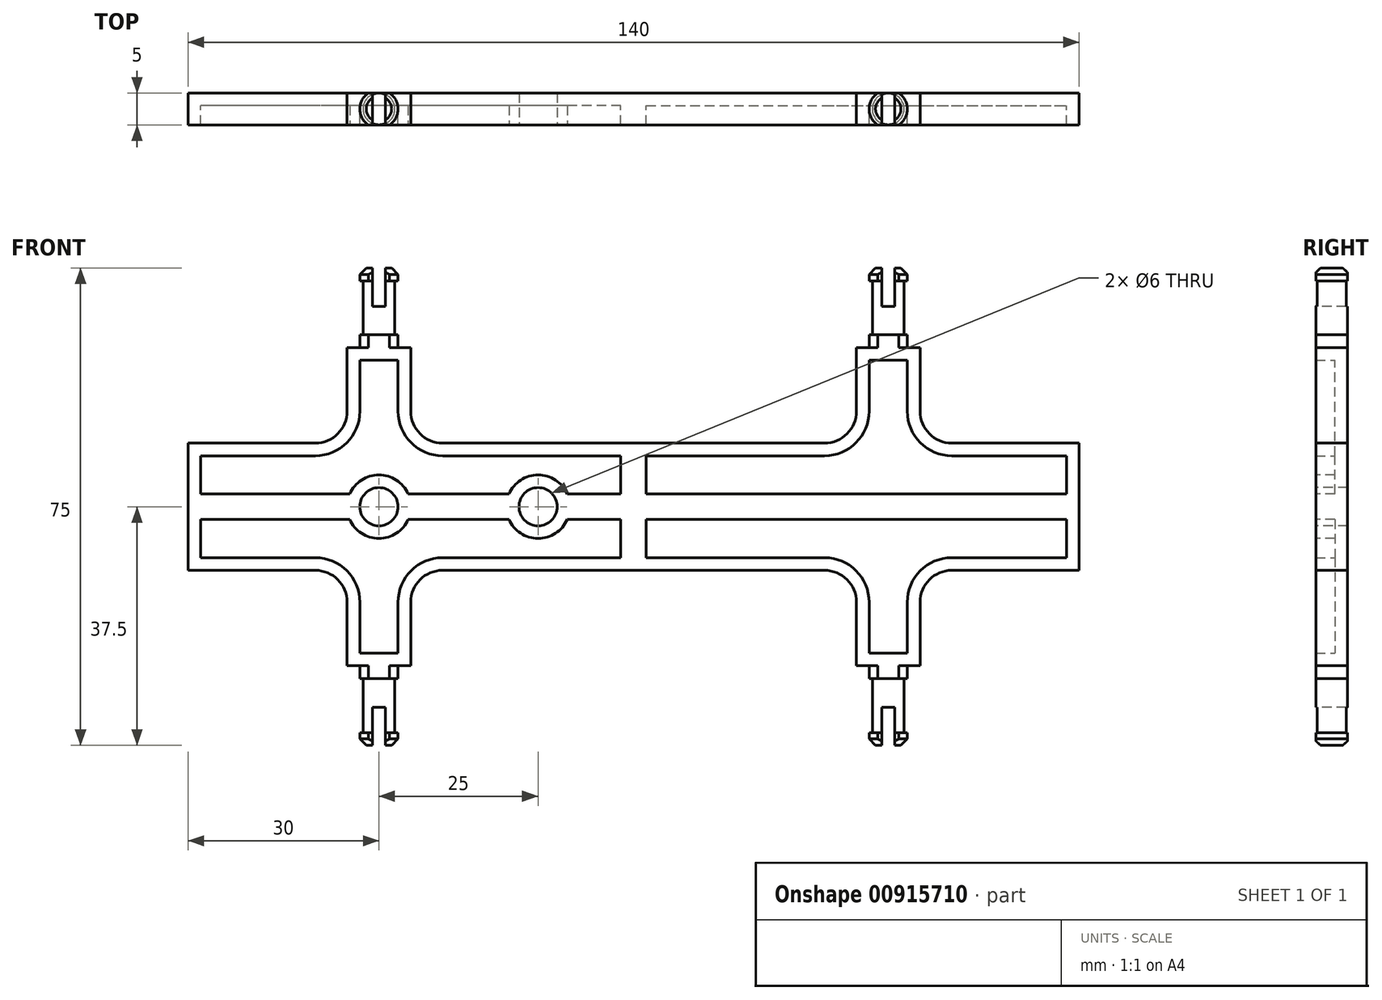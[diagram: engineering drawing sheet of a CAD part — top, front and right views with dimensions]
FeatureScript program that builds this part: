
annotation { "Feature Type Name" : "Feature", "Feature Type Description" : "" }
export const myFeature = defineFeature(function(context is Context, id is Id, definition is map)
    precondition{}
    {
        {
            var Q0;
            Q0=qCreatedBy(makeId("Front.planeOp"),FACE);
            var sketch = newSketch(context, id + "F0", { "sketchPlane" : qUnion([Q0])});
            skLineSegment(sketch, "E0.bottom", {"start": v(0, 0) * mm, "end": v(70, 0) * mm});
            skLineSegment(sketch, "E0.top", {"start": v(0, 10) * mm, "end": v(30, 10) * mm});
            skLineSegment(sketch, "E0.left", {"start": v(0, 0) * mm, "end": v(0, 10) * mm});
            skLineSegment(sketch, "E0.right", {"start": v(70, 0) * mm, "end": v(70, 10) * mm});
            skLineSegment(sketch, "E1.top", {"start": v(35, 25) * mm, "end": v(45, 25) * mm});
            skLineSegment(sketch, "E1.left", {"start": v(35, 15) * mm, "end": v(35, 25) * mm});
            skLineSegment(sketch, "E1.right", {"start": v(45, 15) * mm, "end": v(45, 25) * mm});
            skLineSegment(sketch, "E2.trimOffspring", {"start": v(50, 10) * mm, "end": v(70, 10) * mm});
            skPoint(sketch, "E3.visualSharp", {"position": v(35, 10) * mm});
            skArc(sketch, "E3.filletArc", {"start": v(30, 10) * mm, "mid": v(33.54, 11.46) * mm, "end": v(35, 15) * mm});
            skPoint(sketch, "E4.visualSharp", {"position": v(45, 10) * mm});
            skArc(sketch, "E4.filletArc", {"start": v(45, 15) * mm, "mid": v(46.46, 11.46) * mm, "end": v(50, 10) * mm});
            skSolve(sketch);
        }
        {
            var Q0;
            Q0 = qSketchRegion(id + "F0", true);
            extrude(context, id + "F1", {"entities" : qUnion([Q0]), "endBound" : BoundingType.SYMMETRIC, "depth" : 5 * mm, "offsetDistance" : 25 * mm});
        }
        {
            var Q0;
            Q0=makeQuery(id+"F1.opExtrude","CAP_FACE",FACE,{"disambiguationData":[OSD([sQuery(id+"F0.wireOp",EDGE,"E0.bottom"),sQuery(id+"F0.wireOp",EDGE,"E0.top"),sQuery(id+"F0.wireOp",EDGE,"E0.left"),sQuery(id+"F0.wireOp",EDGE,"E0.right"),sQuery(id+"F0.wireOp",EDGE,"E1.top"),sQuery(id+"F0.wireOp",EDGE,"E1.left"),sQuery(id+"F0.wireOp",EDGE,"E1.right"),sQuery(id+"F0.wireOp",EDGE,"E2.trimOffspring"),sQuery(id+"F0.wireOp",EDGE,"E3.filletArc"),sQuery(id+"F0.wireOp",EDGE,"E4.filletArc")])],"isStart":false});
            shell(context, id + "F2", {"entities" : qUnion([Q0]), "thickness" : 2 * mm});
        }
        {
            var Q0;
            Q0=qCreatedBy(makeId("Front.planeOp"),FACE);
            var sketch = newSketch(context, id + "F3", { "sketchPlane" : qUnion([Q0])});
            skLineSegment(sketch, "E5", {"start": v(40, 25) * mm, "end": v(40, 37.5) * mm});
            skLineSegment(sketch, "E6", {"start": v(40, 37.5) * mm, "end": v(37, 37.5) * mm});
            skLineSegment(sketch, "E7", {"start": v(37, 37.5) * mm, "end": v(37, 35.5) * mm});
            skLineSegment(sketch, "E8", {"start": v(37, 35.5) * mm, "end": v(37.5, 35.5) * mm});
            skLineSegment(sketch, "E9", {"start": v(37.5, 35.5) * mm, "end": v(37.5, 27) * mm});
            skLineSegment(sketch, "E10", {"start": v(37.5, 27) * mm, "end": v(37, 27) * mm});
            skLineSegment(sketch, "E11", {"start": v(37, 27) * mm, "end": v(37, 25) * mm});
            skLineSegment(sketch, "E12", {"start": v(37, 25) * mm, "end": v(40, 25) * mm});
            skSolve(sketch);
        }
        {
            var Q0;
            Q0 = qSketchRegion(id + "F3", true);
            var Q1;
            Q1=sQuery(id+"F3.wireOp",EDGE,"E5");
            revolve(context, id + "F4", {"operationType" : NewBodyOperationType.ADD, "surfaceOperationType" : NewSurfaceOperationType.NEW, "entities" : qUnion([Q0]), "axis" : qUnion([Q1]), "revolveType" : RevolveType.FULL});
        }
        {
            var Q0;
            Q0=makeQuery(id+"F4.opRevolve","SWEPT_EDGE",EDGE,{"disambiguationData":[OSD([sQuery(id+"F3.wireOp",EDGE,"E6"),sQuery(id+"F3.wireOp",EDGE,"E7")])]});
            chamfer(context, id + "F5", {"entities" : qUnion([Q0]), "width" : 1 * mm, "tangentPropagation" : true});
        }
        {
            var Q0;
            Q0=makeQuery(id+"F4.opRevolve","SWEPT_FACE",FACE,{"disambiguationData":[OSD([sQuery(id+"F3.wireOp",EDGE,"E6")])]});
            var sketch = newSketch(context, id + "F6", { "sketchPlane" : qUnion([Q0])});
            skLineSegment(sketch, "E13.bottom", {"start": v(-1.45, 2.5) * mm, "end": v(71.88, 2.5) * mm});
            skLineSegment(sketch, "E13.top", {"start": v(-1.45, -2.5) * mm, "end": v(71.88, -2.5) * mm});
            skLineSegment(sketch, "E13.left", {"start": v(-1.45, 2.5) * mm, "end": v(-1.45, -2.5) * mm});
            skLineSegment(sketch, "E13.right", {"start": v(71.88, 2.5) * mm, "end": v(71.88, -2.5) * mm});
            skSolve(sketch);
        }
        {
            var Q0;
            Q0 = qSketchRegion(id + "F6", true);
            extrude(context, id + "F7", {"entities" : qUnion([Q0]), "operationType" : NewBodyOperationType.INTERSECT, "endBound" : BoundingType.THROUGH_ALL, "oppositeDirection" : true, "depth" : 25 * mm, "offsetDistance" : 25 * mm});
        }
        {
            var Q0;
            Q0=makeQuery(id+"F4.opRevolve","SWEPT_FACE",FACE,{"disambiguationData":[OSD([sQuery(id+"F3.wireOp",EDGE,"E6")])]});
            var sketch = newSketch(context, id + "F8", { "sketchPlane" : qUnion([Q0])});
            skLineSegment(sketch, "E14.bottom", {"start": v(39, 2.85) * mm, "end": v(41, 2.85) * mm});
            skLineSegment(sketch, "E14.top", {"start": v(39, -3.9) * mm, "end": v(41, -3.9) * mm});
            skLineSegment(sketch, "E14.left", {"start": v(39, 2.85) * mm, "end": v(39, -3.9) * mm});
            skLineSegment(sketch, "E14.right", {"start": v(41, 2.85) * mm, "end": v(41, -3.9) * mm});
            skSolve(sketch);
        }
        {
            var Q0;
            Q0 = qSketchRegion(id + "F8", true);
            extrude(context, id + "F9", {"entities" : qUnion([Q0]), "operationType" : NewBodyOperationType.REMOVE, "oppositeDirection" : true, "depth" : 6 * mm, "offsetDistance" : 25 * mm});
        }
        {
            var Q0;
            Q0=makeQuery(id+"F1.opExtrude","SWEPT_BODY",BODY,{"disambiguationData":[OSD([sQuery(id+"F0.wireOp",EDGE,"E0.bottom"),sQuery(id+"F0.wireOp",EDGE,"E0.top"),sQuery(id+"F0.wireOp",EDGE,"E0.left"),sQuery(id+"F0.wireOp",EDGE,"E0.right"),sQuery(id+"F0.wireOp",EDGE,"E1.top"),sQuery(id+"F0.wireOp",EDGE,"E1.left"),sQuery(id+"F0.wireOp",EDGE,"E1.right"),sQuery(id+"F0.wireOp",EDGE,"E2.trimOffspring"),sQuery(id+"F0.wireOp",EDGE,"E3.filletArc"),sQuery(id+"F0.wireOp",EDGE,"E4.filletArc")])]});
            var Q1;
            Q1=qCreatedBy(makeId("Top.planeOp"),FACE);
            mirror(context, id + "F10", {"operationType" : NewBodyOperationType.ADD, "entities" : qUnion([Q0]), "mirrorPlane" : qUnion([Q1])});
        }
        {
            var Q0;
            Q0=makeQuery(id+"F1.opExtrude","SWEPT_BODY",BODY,{"disambiguationData":[OSD([sQuery(id+"F0.wireOp",EDGE,"E0.bottom"),sQuery(id+"F0.wireOp",EDGE,"E0.top"),sQuery(id+"F0.wireOp",EDGE,"E0.left"),sQuery(id+"F0.wireOp",EDGE,"E0.right"),sQuery(id+"F0.wireOp",EDGE,"E1.top"),sQuery(id+"F0.wireOp",EDGE,"E1.left"),sQuery(id+"F0.wireOp",EDGE,"E1.right"),sQuery(id+"F0.wireOp",EDGE,"E2.trimOffspring"),sQuery(id+"F0.wireOp",EDGE,"E3.filletArc"),sQuery(id+"F0.wireOp",EDGE,"E4.filletArc")])]});
            var Q1;
            Q1=qCreatedBy(makeId("Right.planeOp"),FACE);
            mirror(context, id + "F11", {"operationType" : NewBodyOperationType.ADD, "entities" : qUnion([Q0]), "mirrorPlane" : qUnion([Q1])});
        }
        {
            var Q0;
            {var subQ0=makeQuery(id+"F7.boolean.opBoolean","MERGE",FACE,{"derivedFrom":[makeQuery(id+"F1.opExtrude","CAP_FACE",FACE,{"disambiguationData":[OSD([sQuery(id+"F0.wireOp",EDGE,"E0.bottom"),sQuery(id+"F0.wireOp",EDGE,"E0.top"),sQuery(id+"F0.wireOp",EDGE,"E0.left"),sQuery(id+"F0.wireOp",EDGE,"E0.right"),sQuery(id+"F0.wireOp",EDGE,"E1.top"),sQuery(id+"F0.wireOp",EDGE,"E1.left"),sQuery(id+"F0.wireOp",EDGE,"E1.right"),sQuery(id+"F0.wireOp",EDGE,"E2.trimOffspring"),sQuery(id+"F0.wireOp",EDGE,"E3.filletArc"),sQuery(id+"F0.wireOp",EDGE,"E4.filletArc")])],"isStart":false})],"fromTools":[makeQuery(id+"F7.boolean.toolComplement.opBoolean","COPY",FACE,{"derivedFrom":makeQuery(id+"F7.opExtrude","SWEPT_FACE",FACE,{"disambiguationData":[OSD([sQuery(id+"F6.wireOp",EDGE,"E13.top")])]})})]});var subQ1=makeQuery(id+"F10.boolean.opBoolean","MERGE",FACE,{"derivedFrom":[subQ0,makeQuery(id+"F10.opPattern","COPY",FACE,{"derivedFrom":subQ0,"instanceName":"1"})]});Q0=makeQuery(id+"F11.boolean.opBoolean","MERGE",FACE,{"derivedFrom":[subQ1,makeQuery(id+"F11.opPattern","COPY",FACE,{"derivedFrom":subQ1,"instanceName":"1"})]});}
            var sketch = newSketch(context, id + "F12", { "sketchPlane" : qUnion([Q0])});
            skCircle(sketch, "E15", {"center": v(-40, 0) * mm, "radius": 5 * mm});
            skCircle(sketch, "E16", {"center": v(-15, 0) * mm, "radius": 5 * mm});
            skSolve(sketch);
        }
        {
            var Q0;
            Q0 = qSketchRegion(id + "F12", true);
            extrude(context, id + "F13", {"entities" : qUnion([Q0]), "operationType" : NewBodyOperationType.ADD, "endBound" : BoundingType.UP_TO_NEXT, "oppositeDirection" : true, "depth" : 4 * mm, "offsetDistance" : 25 * mm});
        }
        {
            var Q0;
            {var subQ0=makeQuery(id+"F7.boolean.opBoolean","MERGE",FACE,{"derivedFrom":[makeQuery(id+"F1.opExtrude","CAP_FACE",FACE,{"disambiguationData":[OSD([sQuery(id+"F0.wireOp",EDGE,"E0.bottom"),sQuery(id+"F0.wireOp",EDGE,"E0.top"),sQuery(id+"F0.wireOp",EDGE,"E0.left"),sQuery(id+"F0.wireOp",EDGE,"E0.right"),sQuery(id+"F0.wireOp",EDGE,"E1.top"),sQuery(id+"F0.wireOp",EDGE,"E1.left"),sQuery(id+"F0.wireOp",EDGE,"E1.right"),sQuery(id+"F0.wireOp",EDGE,"E2.trimOffspring"),sQuery(id+"F0.wireOp",EDGE,"E3.filletArc"),sQuery(id+"F0.wireOp",EDGE,"E4.filletArc")])],"isStart":false})],"fromTools":[makeQuery(id+"F7.boolean.toolComplement.opBoolean","COPY",FACE,{"derivedFrom":makeQuery(id+"F7.opExtrude","SWEPT_FACE",FACE,{"disambiguationData":[OSD([sQuery(id+"F6.wireOp",EDGE,"E13.top")])]})})]});var subQ1=makeQuery(id+"F10.boolean.opBoolean","MERGE",FACE,{"derivedFrom":[subQ0,makeQuery(id+"F10.opPattern","COPY",FACE,{"derivedFrom":subQ0,"instanceName":"1"})]});Q0=makeQuery(id+"F13.boolean.opBoolean","MERGE",FACE,{"derivedFrom":[makeQuery(id+"F11.boolean.opBoolean","MERGE",FACE,{"derivedFrom":[subQ1,makeQuery(id+"F11.opPattern","COPY",FACE,{"derivedFrom":subQ1,"instanceName":"1"})]}),makeQuery(id+"F13.opExtrude","CAP_FACE",FACE,{"disambiguationData":[OSD([sQuery(id+"F12.wireOp",EDGE,"E15")])],"isStart":true}),makeQuery(id+"F13.opExtrude","CAP_FACE",FACE,{"disambiguationData":[OSD([sQuery(id+"F12.wireOp",EDGE,"E16")])],"isStart":true})]});}
            var sketch = newSketch(context, id + "F14", { "sketchPlane" : qUnion([Q0])});
            skPoint(sketch, "E17", {"position": v(-40, 0) * mm});
            skPoint(sketch, "E18", {"position": v(-15, 0) * mm});
            skSolve(sketch);
        }
        {
            var Q0;
            Q0=sQuery(id+"F14.wireOp",VERTEX,"E17");
            var Q1;
            Q1=sQuery(id+"F14.wireOp",VERTEX,"E18");
            var Q2;
            Q2=makeQuery(id+"F1.opExtrude","SWEPT_BODY",BODY,{"disambiguationData":[OSD([sQuery(id+"F0.wireOp",EDGE,"E0.bottom"),sQuery(id+"F0.wireOp",EDGE,"E0.top"),sQuery(id+"F0.wireOp",EDGE,"E0.left"),sQuery(id+"F0.wireOp",EDGE,"E0.right"),sQuery(id+"F0.wireOp",EDGE,"E1.top"),sQuery(id+"F0.wireOp",EDGE,"E1.left"),sQuery(id+"F0.wireOp",EDGE,"E1.right"),sQuery(id+"F0.wireOp",EDGE,"E2.trimOffspring"),sQuery(id+"F0.wireOp",EDGE,"E3.filletArc"),sQuery(id+"F0.wireOp",EDGE,"E4.filletArc")])]});
            hole(context, id + "F15", {"style" : HoleStyle.SIMPLE, "endStyle" : HoleEndStyle.THROUGH, "holeDiameter" : 6 * mm, "majorDiameter" : 5 * mm, "isTappedThrough" : true, "tappedDepth" : 12 * mm, "tapClearance" : 3, "locations" : qUnion([Q0, Q1]), "scope" : qUnion([Q2])});
        }
    });
